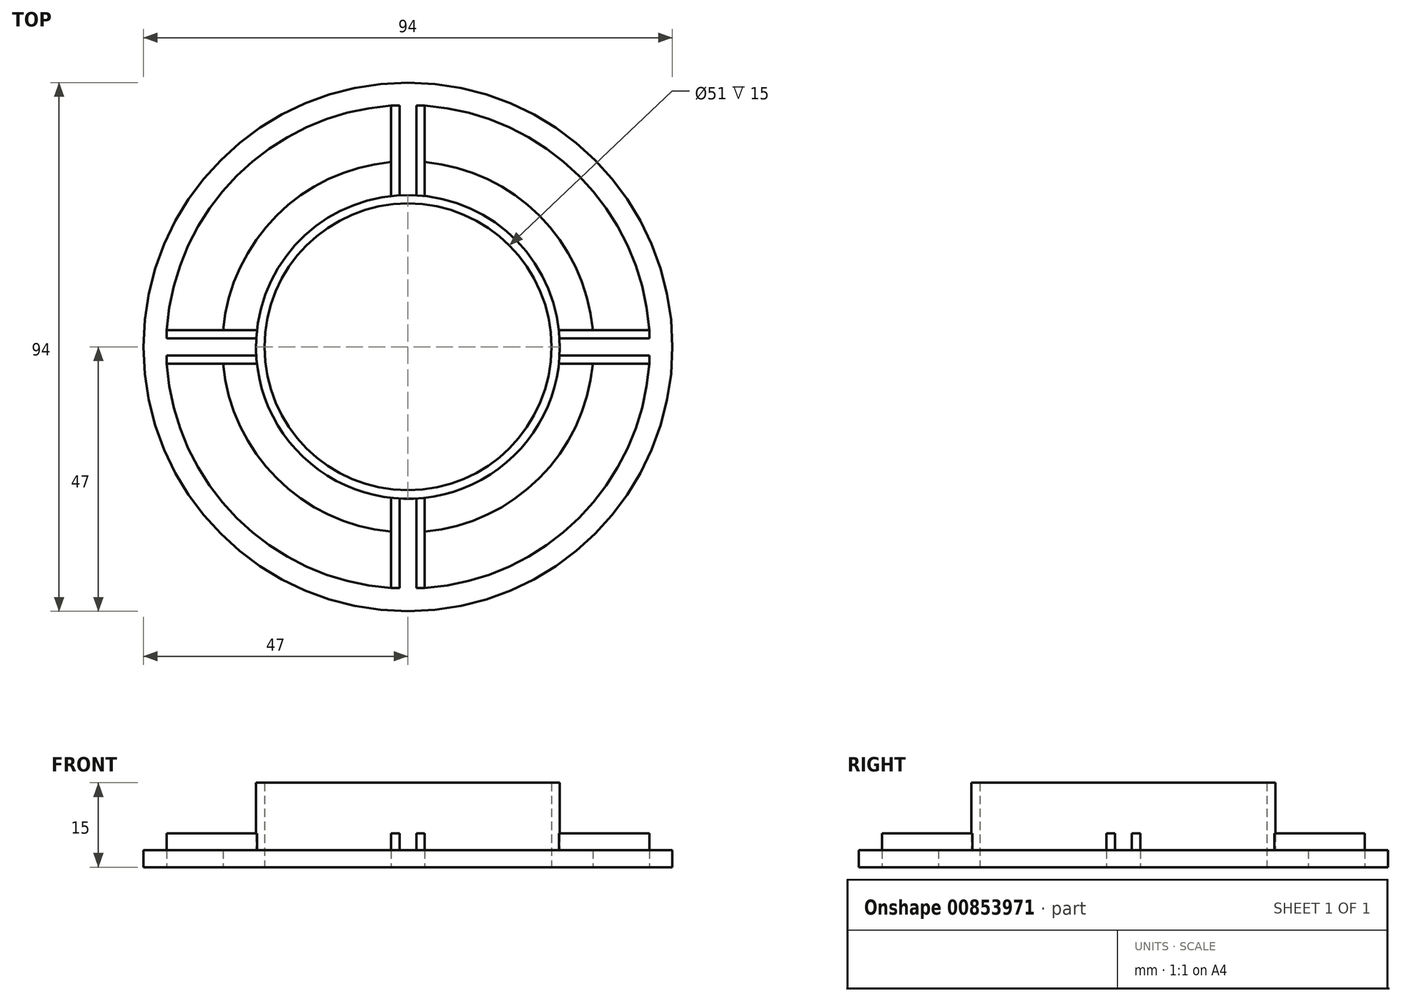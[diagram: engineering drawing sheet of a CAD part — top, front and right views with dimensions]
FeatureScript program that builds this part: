
annotation { "Feature Type Name" : "Feature", "Feature Type Description" : "" }
export const myFeature = defineFeature(function(context is Context, id is Id, definition is map)
    precondition{}
    {
        {
            var Q0;
            Q0=qCreatedBy(makeId("Top.planeOp"),FACE);
            var sketch = newSketch(context, id + "F0", { "sketchPlane" : qUnion([Q0])});
            skCircle(sketch, "E0", {"center": v(0, 0) * mm, "radius": 27 * mm});
            skCircle(sketch, "E1.0", {"center": v(0, 0) * mm, "radius": 25.5 * mm});
            skCircle(sketch, "E2.0", {"center": v(0, 0) * mm, "radius": 47 * mm});
            skArc(sketch, "E3.0", {"start": v(-42.9, -3) * mm, "mid": v(-30.4, -30.4) * mm, "end": v(-3, -42.9) * mm});
            skArc(sketch, "E4.0", {"start": v(-32.86, -3) * mm, "mid": v(-23.33, -23.33) * mm, "end": v(-3, -32.86) * mm});
            skLineSegment(sketch, "E5", {"start": v(-32.86, 3) * mm, "end": v(-42.9, 3) * mm});
            skLineSegment(sketch, "E6", {"start": v(-32.86, -3) * mm, "end": v(-42.9, -3) * mm});
            skLineSegment(sketch, "E7", {"start": v(32.86, 3) * mm, "end": v(42.9, 3) * mm});
            skLineSegment(sketch, "E8", {"start": v(32.86, -3) * mm, "end": v(42.9, -3) * mm});
            skLineSegment(sketch, "E9", {"start": v(-3, 42.9) * mm, "end": v(-3, 32.86) * mm});
            skLineSegment(sketch, "E10", {"start": v(3, 42.9) * mm, "end": v(3, 32.86) * mm});
            skArc(sketch, "E11.trimOffspring", {"start": v(-3, 32.86) * mm, "mid": v(-23.33, 23.33) * mm, "end": v(-32.86, 3) * mm});
            skArc(sketch, "E12.trimOffspring", {"start": v(32.86, 3) * mm, "mid": v(23.33, 23.33) * mm, "end": v(3, 32.86) * mm});
            skArc(sketch, "E13.trimOffspring", {"start": v(42.9, 3) * mm, "mid": v(30.4, 30.4) * mm, "end": v(3, 42.9) * mm});
            skArc(sketch, "E14.trimOffspring", {"start": v(-3, 42.9) * mm, "mid": v(-30.4, 30.4) * mm, "end": v(-42.9, 3) * mm});
            skLineSegment(sketch, "E15", {"start": v(-3, -32.86) * mm, "end": v(-3, -42.9) * mm});
            skLineSegment(sketch, "E16", {"start": v(3, -32.86) * mm, "end": v(3, -42.9) * mm});
            skArc(sketch, "E17.trimOffspring", {"start": v(3, -32.86) * mm, "mid": v(23.33, -23.33) * mm, "end": v(32.86, -3) * mm});
            skArc(sketch, "E18.trimOffspring", {"start": v(3, -42.9) * mm, "mid": v(30.4, -30.4) * mm, "end": v(42.9, -3) * mm});
            skSolve(sketch);
        }
        {
            var Q0;
            Q0=makeQuery(id+"F0.imprint","IMPRINT",FACE,{"disambiguationData":[TD([[makeQuery(id+"F0.imprint","IMPRINT",EDGE,{"derivedFrom":sQuery(id+"F0.wireOp",EDGE,"E0")}),1.0]])]});
            extrude(context, id + "F1", {"entities" : qUnion([Q0]), "depth" : 15 * mm, "offsetDistance" : 25 * mm});
        }
        {
            var Q0;
            Q0 = qSketchRegion(id + "F0", true);
            extrude(context, id + "F2", {"entities" : qUnion([Q0]), "operationType" : NewBodyOperationType.ADD, "depth" : 3 * mm, "offsetDistance" : 25 * mm});
        }
        {
            var Q0;
            Q0=makeQuery(id+"F2.opExtrude","CAP_FACE",FACE,{"disambiguationData":[OSD([sQuery(id+"F0.wireOp",EDGE,"E0"),sQuery(id+"F0.wireOp",EDGE,"E2.0"),sQuery(id+"F0.wireOp",EDGE,"E3.0"),sQuery(id+"F0.wireOp",EDGE,"E4.0"),sQuery(id+"F0.wireOp",EDGE,"E5"),sQuery(id+"F0.wireOp",EDGE,"E6"),sQuery(id+"F0.wireOp",EDGE,"E7"),sQuery(id+"F0.wireOp",EDGE,"E8"),sQuery(id+"F0.wireOp",EDGE,"E9"),sQuery(id+"F0.wireOp",EDGE,"E10"),sQuery(id+"F0.wireOp",EDGE,"E11.trimOffspring"),sQuery(id+"F0.wireOp",EDGE,"E12.trimOffspring"),sQuery(id+"F0.wireOp",EDGE,"E13.trimOffspring"),sQuery(id+"F0.wireOp",EDGE,"E14.trimOffspring"),sQuery(id+"F0.wireOp",EDGE,"E15"),sQuery(id+"F0.wireOp",EDGE,"E16"),sQuery(id+"F0.wireOp",EDGE,"E17.trimOffspring"),sQuery(id+"F0.wireOp",EDGE,"E18.trimOffspring")])],"isStart":false});
            var sketch = newSketch(context, id + "F3", { "sketchPlane" : qUnion([Q0])});
            skLineSegment(sketch, "E19.bottom", {"start": v(-26.83, 1.5) * mm, "end": v(-42.9, 1.5) * mm});
            skLineSegment(sketch, "E19.top", {"start": v(-26.83, 3) * mm, "end": v(-42.9, 3) * mm});
            skLineSegment(sketch, "E19.left", {"start": v(-26.83, 1.5) * mm, "end": v(-26.83, 3) * mm});
            skLineSegment(sketch, "E19.right", {"start": v(-42.9, 1.5) * mm, "end": v(-42.9, 3) * mm});
            skLineSegment(sketch, "E20.bottom", {"start": v(-26.83, -1.5) * mm, "end": v(-42.9, -1.5) * mm});
            skLineSegment(sketch, "E20.top", {"start": v(-26.83, -3) * mm, "end": v(-42.9, -3) * mm});
            skLineSegment(sketch, "E20.left", {"start": v(-26.83, -1.5) * mm, "end": v(-26.83, -3) * mm});
            skLineSegment(sketch, "E20.right", {"start": v(-42.9, -1.5) * mm, "end": v(-42.9, -3) * mm});
            skLineSegment(sketch, "E21.bottom", {"start": v(26.83, 1.5) * mm, "end": v(42.9, 1.5) * mm});
            skLineSegment(sketch, "E21.top", {"start": v(26.83, 3) * mm, "end": v(42.9, 3) * mm});
            skLineSegment(sketch, "E21.left", {"start": v(26.83, 1.5) * mm, "end": v(26.83, 3) * mm});
            skLineSegment(sketch, "E21.right", {"start": v(42.9, 1.5) * mm, "end": v(42.9, 3) * mm});
            skLineSegment(sketch, "E22.bottom", {"start": v(26.83, -1.5) * mm, "end": v(42.9, -1.5) * mm});
            skLineSegment(sketch, "E22.top", {"start": v(26.83, -3) * mm, "end": v(42.9, -3) * mm});
            skLineSegment(sketch, "E22.left", {"start": v(26.83, -1.5) * mm, "end": v(26.83, -3) * mm});
            skLineSegment(sketch, "E22.right", {"start": v(42.9, -1.5) * mm, "end": v(42.9, -3) * mm});
            skLineSegment(sketch, "E23.bottom", {"start": v(-1.5, 26.83) * mm, "end": v(-3, 26.83) * mm});
            skLineSegment(sketch, "E23.top", {"start": v(-1.5, 42.9) * mm, "end": v(-3, 42.9) * mm});
            skLineSegment(sketch, "E23.left", {"start": v(-1.5, 26.83) * mm, "end": v(-1.5, 42.9) * mm});
            skLineSegment(sketch, "E23.right", {"start": v(-3, 26.83) * mm, "end": v(-3, 42.9) * mm});
            skLineSegment(sketch, "E24.bottom", {"start": v(1.5, 26.83) * mm, "end": v(3, 26.83) * mm});
            skLineSegment(sketch, "E24.top", {"start": v(1.5, 42.9) * mm, "end": v(3, 42.9) * mm});
            skLineSegment(sketch, "E24.left", {"start": v(1.5, 26.83) * mm, "end": v(1.5, 42.9) * mm});
            skLineSegment(sketch, "E24.right", {"start": v(3, 26.83) * mm, "end": v(3, 42.9) * mm});
            skLineSegment(sketch, "E25.bottom", {"start": v(-1.5, -26.83) * mm, "end": v(-3, -26.83) * mm});
            skLineSegment(sketch, "E25.top", {"start": v(-1.5, -42.9) * mm, "end": v(-3, -42.9) * mm});
            skLineSegment(sketch, "E25.left", {"start": v(-1.5, -26.83) * mm, "end": v(-1.5, -42.9) * mm});
            skLineSegment(sketch, "E25.right", {"start": v(-3, -26.83) * mm, "end": v(-3, -42.9) * mm});
            skLineSegment(sketch, "E26.bottom", {"start": v(1.5, -26.83) * mm, "end": v(3, -26.83) * mm});
            skLineSegment(sketch, "E26.top", {"start": v(1.5, -42.9) * mm, "end": v(3, -42.9) * mm});
            skLineSegment(sketch, "E26.left", {"start": v(1.5, -26.83) * mm, "end": v(1.5, -42.9) * mm});
            skLineSegment(sketch, "E26.right", {"start": v(3, -26.83) * mm, "end": v(3, -42.9) * mm});
            skCircle(sketch, "E27.0", {"center": v(0, 0) * mm, "radius": 27 * mm, "construction": true});
            skPoint(sketch, "E28.0", {"position": v(-42.9, 3) * mm});
            skPoint(sketch, "E29.0", {"position": v(-42.9, -3) * mm});
            skPoint(sketch, "E30.0", {"position": v(42.9, 3) * mm});
            skPoint(sketch, "E31.0", {"position": v(42.9, -3) * mm});
            skPoint(sketch, "E32.0", {"position": v(-3, 42.9) * mm});
            skPoint(sketch, "E33.0", {"position": v(3, 42.9) * mm});
            skPoint(sketch, "E34.0", {"position": v(-3, -42.9) * mm});
            skPoint(sketch, "E35.0", {"position": v(3, -42.9) * mm});
            skSolve(sketch);
        }
        {
            var Q0;
            Q0 = qSketchRegion(id + "F3", true);
            extrude(context, id + "F4", {"entities" : qUnion([Q0]), "operationType" : NewBodyOperationType.ADD, "depth" : 3 * mm, "offsetDistance" : 25 * mm});
        }
        {
            var Q0;
            Q0 = qSketchRegion(id + "F3", true);
            extrude(context, id + "F5", {"entities" : qUnion([Q0]), "operationType" : NewBodyOperationType.ADD, "oppositeDirection" : true, "depth" : 3 * mm, "offsetDistance" : 25 * mm});
        }
    });
